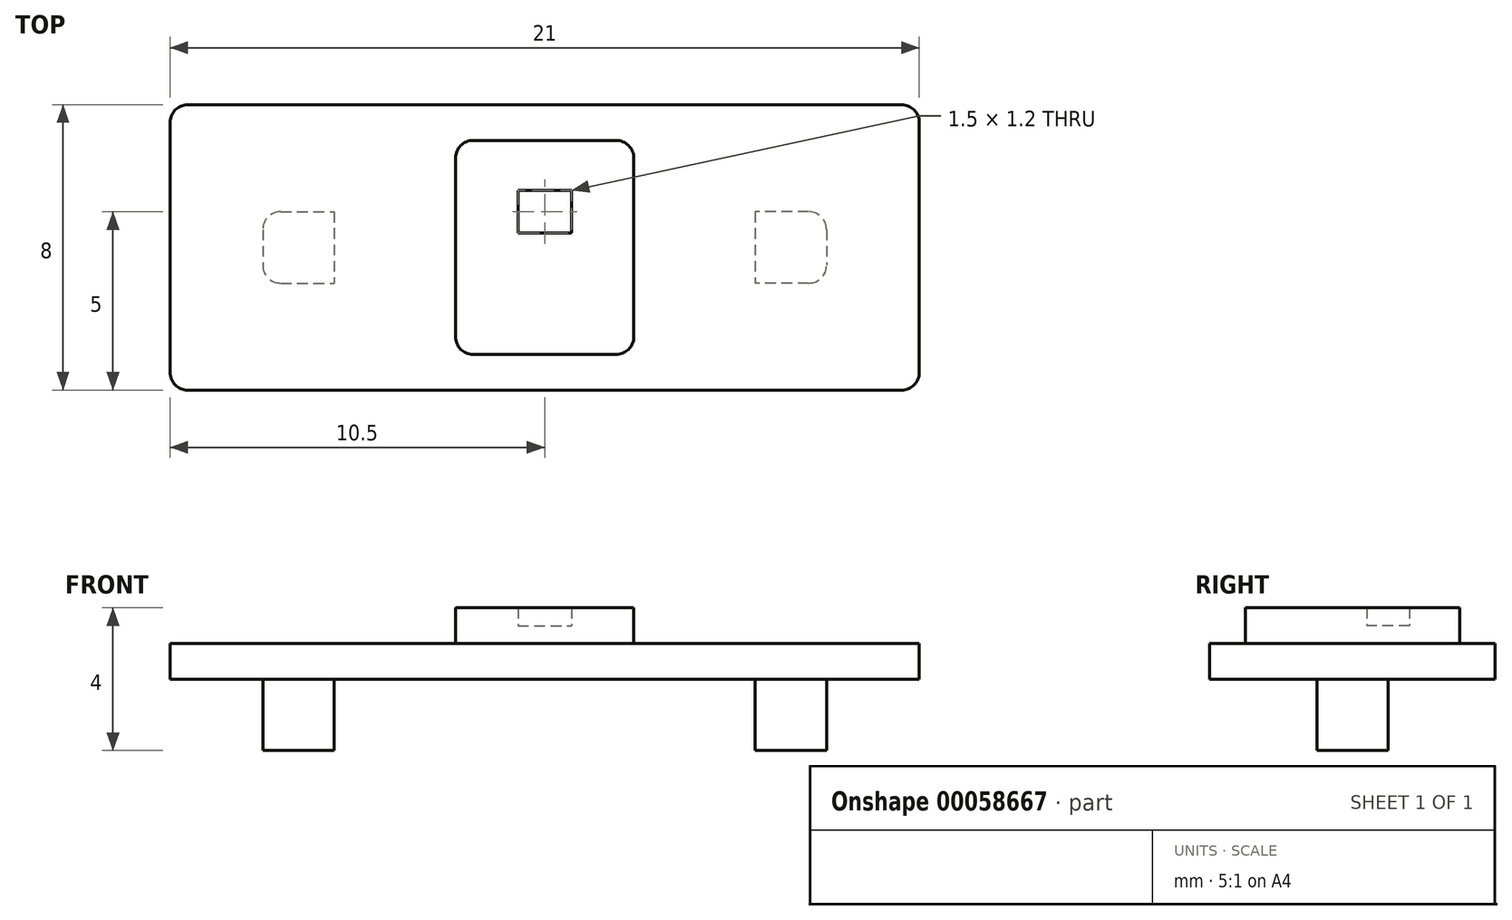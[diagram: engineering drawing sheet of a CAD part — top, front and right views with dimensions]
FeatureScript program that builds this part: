
annotation { "Feature Type Name" : "Feature", "Feature Type Description" : "" }
export const myFeature = defineFeature(function(context is Context, id is Id, definition is map)
    precondition{}
    {
        {
            var Q0;
            Q0=qCreatedBy(makeId("Top.planeOp"),FACE);
            var sketch = newSketch(context, id + "F0", { "sketchPlane" : qUnion([Q0])});
            skLineSegment(sketch, "E0.rect.bottom", {"start": v(-10, 4) * mm, "end": v(10, 4) * mm});
            skLineSegment(sketch, "E0.rect.top", {"start": v(-10, -4) * mm, "end": v(10, -4) * mm});
            skLineSegment(sketch, "E0.rect.left", {"start": v(-10.5, 3.5) * mm, "end": v(-10.5, -3.5) * mm});
            skLineSegment(sketch, "E0.rect.right", {"start": v(10.5, 3.5) * mm, "end": v(10.5, -3.5) * mm});
            skPoint(sketch, "E0.rect.middle", {"position": v(0, 0) * mm});
            skLineSegment(sketch, "E1.rect.bottom", {"start": v(-7.4, 1) * mm, "end": v(-5.9, 1) * mm});
            skLineSegment(sketch, "E1.rect.top", {"start": v(-7.4, -1) * mm, "end": v(-5.9, -1) * mm});
            skLineSegment(sketch, "E1.rect.left", {"start": v(-7.9, 0.5) * mm, "end": v(-7.9, -0.5) * mm});
            skLineSegment(sketch, "E1.rect.right", {"start": v(-5.9, 1) * mm, "end": v(-5.9, -1) * mm});
            skPoint(sketch, "E1.rect.middle", {"position": v(-6.9, 0) * mm});
            skLineSegment(sketch, "E2.MirrorCS", {"start": v(5.9, 1) * mm, "end": v(5.9, -1) * mm});
            skLineSegment(sketch, "E3.MirrorCS", {"start": v(7.4, 1) * mm, "end": v(5.9, 1) * mm});
            skLineSegment(sketch, "E4.MirrorCS", {"start": v(7.9, 0.5) * mm, "end": v(7.9, -0.5) * mm});
            skLineSegment(sketch, "E5.MirrorCS", {"start": v(7.4, -1) * mm, "end": v(5.9, -1) * mm});
            skLineSegment(sketch, "E6.rect.bottom", {"start": v(2, 3) * mm, "end": v(-2, 3) * mm});
            skLineSegment(sketch, "E6.rect.top", {"start": v(2, -3) * mm, "end": v(-2, -3) * mm});
            skLineSegment(sketch, "E6.rect.left", {"start": v(2.5, 2.5) * mm, "end": v(2.5, -2.5) * mm});
            skLineSegment(sketch, "E6.rect.right", {"start": v(-2.5, 2.5) * mm, "end": v(-2.5, -2.5) * mm});
            skPoint(sketch, "E7.visualSharp", {"position": v(-7.9, 1) * mm});
            skArc(sketch, "E7.filletArc", {"start": v(-7.4, 1) * mm, "mid": v(-7.75, 0.85) * mm, "end": v(-7.9, 0.5) * mm});
            skPoint(sketch, "E8.visualSharp", {"position": v(-7.9, -1) * mm});
            skArc(sketch, "E8.filletArc", {"start": v(-7.9, -0.5) * mm, "mid": v(-7.75, -0.85) * mm, "end": v(-7.4, -1) * mm});
            skPoint(sketch, "E9.visualSharp", {"position": v(7.9, 1) * mm});
            skArc(sketch, "E9.filletArc", {"start": v(7.9, 0.5) * mm, "mid": v(7.75, 0.85) * mm, "end": v(7.4, 1) * mm});
            skPoint(sketch, "E10.visualSharp", {"position": v(7.9, -1) * mm});
            skArc(sketch, "E10.filletArc", {"start": v(7.4, -1) * mm, "mid": v(7.75, -0.85) * mm, "end": v(7.9, -0.5) * mm});
            skPoint(sketch, "E11.visualSharp", {"position": v(-10.5, 4) * mm});
            skArc(sketch, "E11.filletArc", {"start": v(-10, 4) * mm, "mid": v(-10.35, 3.85) * mm, "end": v(-10.5, 3.5) * mm});
            skPoint(sketch, "E12.visualSharp", {"position": v(-10.5, -4) * mm});
            skArc(sketch, "E12.filletArc", {"start": v(-10.5, -3.5) * mm, "mid": v(-10.35, -3.85) * mm, "end": v(-10, -4) * mm});
            skPoint(sketch, "E13.visualSharp", {"position": v(10.5, -4) * mm});
            skArc(sketch, "E13.filletArc", {"start": v(10, -4) * mm, "mid": v(10.35, -3.85) * mm, "end": v(10.5, -3.5) * mm});
            skPoint(sketch, "E14.visualSharp", {"position": v(10.5, 4) * mm});
            skArc(sketch, "E14.filletArc", {"start": v(10.5, 3.5) * mm, "mid": v(10.35, 3.85) * mm, "end": v(10, 4) * mm});
            skPoint(sketch, "E15.visualSharp", {"position": v(-2.5, 3) * mm});
            skArc(sketch, "E15.filletArc", {"start": v(-2, 3) * mm, "mid": v(-2.35, 2.85) * mm, "end": v(-2.5, 2.5) * mm});
            skPoint(sketch, "E16.visualSharp", {"position": v(-2.5, -3) * mm});
            skArc(sketch, "E16.filletArc", {"start": v(-2.5, -2.5) * mm, "mid": v(-2.35, -2.85) * mm, "end": v(-2, -3) * mm});
            skPoint(sketch, "E17.visualSharp", {"position": v(2.5, -3) * mm});
            skArc(sketch, "E17.filletArc", {"start": v(2, -3) * mm, "mid": v(2.35, -2.85) * mm, "end": v(2.5, -2.5) * mm});
            skPoint(sketch, "E18.visualSharp", {"position": v(2.5, 3) * mm});
            skArc(sketch, "E18.filletArc", {"start": v(2.5, 2.5) * mm, "mid": v(2.35, 2.85) * mm, "end": v(2, 3) * mm});
            skLineSegment(sketch, "E19.rect.bottom", {"start": v(-0.75, 1.6) * mm, "end": v(0.75, 1.6) * mm});
            skLineSegment(sketch, "E19.rect.top", {"start": v(-0.75, 0.4) * mm, "end": v(0.75, 0.4) * mm});
            skLineSegment(sketch, "E19.rect.left", {"start": v(-0.75, 1.6) * mm, "end": v(-0.75, 0.4) * mm});
            skLineSegment(sketch, "E19.rect.right", {"start": v(0.75, 1.6) * mm, "end": v(0.75, 0.4) * mm});
            skPoint(sketch, "E19.rect.middle", {"position": v(0, 1) * mm});
            skSolve(sketch);
        }
        {
            var Q0;
            Q0=makeQuery(id+"F0.imprint","IMPRINT",FACE,{"disambiguationData":[TD([[makeQuery(id+"F0.imprint","IMPRINT",EDGE,{"derivedFrom":sQuery(id+"F0.wireOp",EDGE,"E0.rect.bottom")}),-1.0]])]});
            extrude(context, id + "F1", {"entities" : qUnion([Q0]), "depth" : 3 * mm, "hasSecondDirection" : true, "secondDirectionOppositeDirection" : false, "secondDirectionDepth" : 2 * mm});
        }
        {
            var Q0;
            Q0=makeQuery(id+"F0.imprint","IMPRINT",FACE,{"disambiguationData":[TD([[makeQuery(id+"F0.imprint","IMPRINT",EDGE,{"derivedFrom":sQuery(id+"F0.wireOp",EDGE,"E1.rect.bottom")}),-1.0]])]});
            var Q1;
            Q1=makeQuery(id+"F0.imprint","IMPRINT",FACE,{"disambiguationData":[TD([[makeQuery(id+"F0.imprint","IMPRINT",EDGE,{"derivedFrom":sQuery(id+"F0.wireOp",EDGE,"E2.MirrorCS")}),1.0]])]});
            extrude(context, id + "F2", {"entities" : qUnion([Q0, Q1]), "operationType" : NewBodyOperationType.ADD, "depth" : 3 * mm});
        }
        {
            var Q0;
            Q0=makeQuery(id+"F0.imprint","IMPRINT",FACE,{"disambiguationData":[TD([[makeQuery(id+"F0.imprint","IMPRINT",EDGE,{"derivedFrom":sQuery(id+"F0.wireOp",EDGE,"30aa7c9f-918b-4e0f-9d93-b022fdfc9aa2.rect.bottom")}),1.0]])]});
            var Q1;
            Q1=makeQuery(id+"F0.imprint","IMPRINT",FACE,{"disambiguationData":[TD([[makeQuery(id+"F0.imprint","IMPRINT",EDGE,{"derivedFrom":sQuery(id+"F0.wireOp",EDGE,"E6.rect.bottom")}),1.0]])]});
            extrude(context, id + "F3", {"entities" : qUnion([Q0, Q1]), "operationType" : NewBodyOperationType.ADD, "depth" : 4 * mm, "hasSecondDirection" : true, "secondDirectionOppositeDirection" : false, "secondDirectionDepth" : 2 * mm});
        }
        {
            var Q0;
            Q0=makeQuery(id+"F0.imprint","IMPRINT",FACE,{"disambiguationData":[TD([[makeQuery(id+"F0.imprint","IMPRINT",EDGE,{"derivedFrom":sQuery(id+"F0.wireOp",EDGE,"E19.rect.bottom")}),-1.0]])]});
            extrude(context, id + "F4", {"entities" : qUnion([Q0]), "depth" : 4 * mm, "hasSecondDirection" : true, "secondDirectionOppositeDirection" : false, "secondDirectionDepth" : 3.5 * mm});
        }
    });
